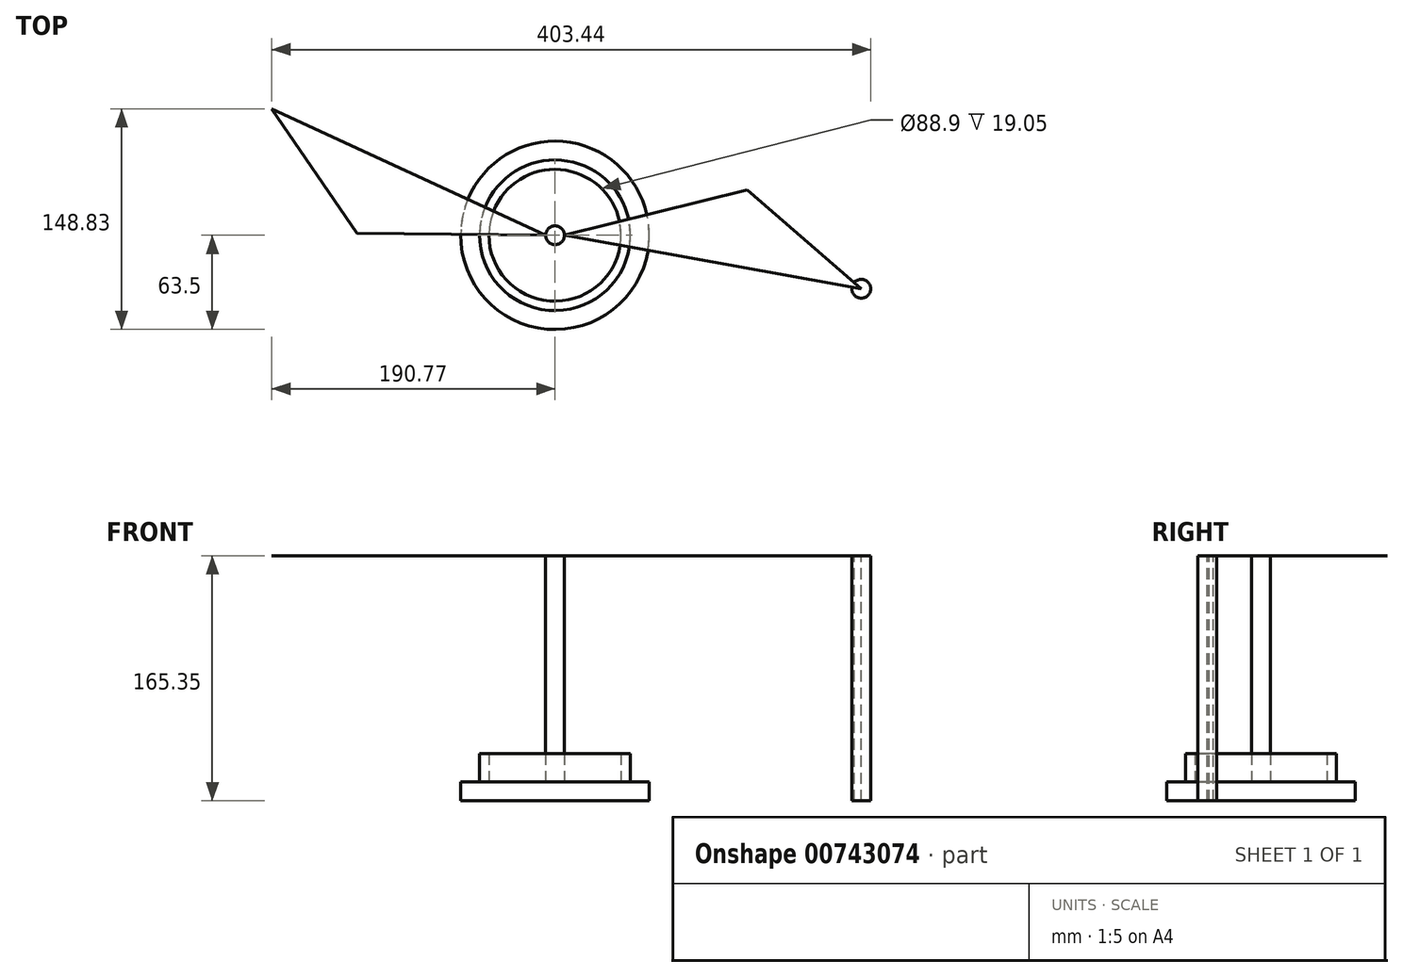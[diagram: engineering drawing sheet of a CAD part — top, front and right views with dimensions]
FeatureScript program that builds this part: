
annotation { "Feature Type Name" : "Feature", "Feature Type Description" : "" }
export const myFeature = defineFeature(function(context is Context, id is Id, definition is map)
    precondition{}
    {
        {
            var Q0;
            Q0=qCreatedBy(makeId("Top.planeOp"),FACE);
            var sketch = newSketch(context, id + "F0", { "sketchPlane" : qUnion([Q0])});
            skCircle(sketch, "E0", {"center": v(0, 0) * mm, "radius": 63.5 * mm});
            skSolve(sketch);
        }
        {
            var Q0;
            Q0 = qSketchRegion(id + "F0", true);
            extrude(context, id + "F1", {"entities" : qUnion([Q0]), "depth" : 12.7 * mm, "offsetDistance" : 25.4 * mm});
        }
        {
            var Q0;
            Q0=qCreatedBy(makeId("Top.planeOp"),FACE);
            var sketch = newSketch(context, id + "F2", { "sketchPlane" : qUnion([Q0])});
            skCircle(sketch, "E1", {"center": v(0, 0) * mm, "radius": 50.8 * mm});
            skCircle(sketch, "E2", {"center": v(0, 0) * mm, "radius": 44.45 * mm});
            skSolve(sketch);
        }
        {
            var Q0;
            Q0 = qSketchRegion(id + "F2", true);
            extrude(context, id + "F3", {"entities" : qUnion([Q0]), "operationType" : NewBodyOperationType.ADD, "depth" : 31.75 * mm, "offsetDistance" : 25.4 * mm});
        }
        {
            var Q0;
            Q0=makeQuery(id+"F3.boolean.opBoolean","SPLIT",FACE,{"disambiguationData":[TD([makeQuery(id+"F3.opExtrude","SWEPT_FACE",FACE,{"disambiguationData":[OSD([sQuery(id+"F2.wireOp",EDGE,"E2")])]})])],"derivedFrom":makeQuery(id+"F1.opExtrude","CAP_FACE",FACE,{"disambiguationData":[OSD([sQuery(id+"F0.wireOp",EDGE,"E0")])],"isStart":false})});
            var sketch = newSketch(context, id + "F4", { "sketchPlane" : qUnion([Q0])});
            skCircle(sketch, "E3", {"center": v(0, 0) * mm, "radius": 6.35 * mm});
            skSolve(sketch);
        }
        {
            var Q0;
            Q0=makeQuery(id+"F4.imprint","IMPRINT",FACE,{"disambiguationData":[TD([[makeQuery(id+"F4.imprint","IMPRINT",EDGE,{"derivedFrom":sQuery(id+"F4.wireOp",EDGE,"E3")}),1.0]])]});
            extrude(context, id + "F5", {"entities" : qUnion([Q0]), "operationType" : NewBodyOperationType.ADD, "depth" : 152.4 * mm, "offsetDistance" : 25.4 * mm});
        }
        {
            var Q0;
            Q0=makeQuery(id+"F5.opExtrude","CAP_FACE",FACE,{"disambiguationData":[OSD([sQuery(id+"F4.wireOp",EDGE,"E3")])],"isStart":false});
            var sketch = newSketch(context, id + "F6", { "sketchPlane" : qUnion([Q0])});
            skLineSegment(sketch, "E4", {"start": v(6.35, 0) * mm, "end": v(129.62, 30.55) * mm});
            skLineSegment(sketch, "E5", {"start": v(6.35, 0) * mm, "end": v(206.32, -36.07) * mm});
            skLineSegment(sketch, "E6", {"start": v(129.62, 30.55) * mm, "end": v(206.32, -36.07) * mm});
            skSolve(sketch);
        }
        {
            var Q0;
            Q0 = qSketchRegion(id + "F6", true);
            extrude(context, id + "F7", {"entities" : qUnion([Q0]), "depth" : 0.25 * mm, "offsetDistance" : 25.4 * mm});
        }
        {
            var Q0;
            Q0=makeQuery(id+"F5.opExtrude","CAP_FACE",FACE,{"disambiguationData":[OSD([sQuery(id+"F4.wireOp",EDGE,"E3")])],"isStart":false});
            var sketch = newSketch(context, id + "F8", { "sketchPlane" : qUnion([Q0])});
            skLineSegment(sketch, "E7", {"start": v(-6.35, 0) * mm, "end": v(-190.77, 85.33) * mm});
            skLineSegment(sketch, "E8", {"start": v(-190.77, 85.33) * mm, "end": v(-133.34, 1.51) * mm});
            skLineSegment(sketch, "E9", {"start": v(-133.34, 1.51) * mm, "end": v(-6.35, 0) * mm});
            skSolve(sketch);
        }
        {
            var Q0;
            Q0=makeQuery(id+"F8.imprint","IMPRINT",FACE,{"disambiguationData":[TD([[makeQuery(id+"F8.imprint","IMPRINT",EDGE,{"derivedFrom":sQuery(id+"F8.wireOp",EDGE,"E7")}),1.0]])]});
            extrude(context, id + "F9", {"entities" : qUnion([Q0]), "depth" : 0.25 * mm, "offsetDistance" : 25.4 * mm});
        }
        {
            var Q0;
            Q0=makeQuery(id+"F9.opExtrude","CAP_FACE",FACE,{"disambiguationData":[OSD([sQuery(id+"F8.wireOp",EDGE,"E7"),sQuery(id+"F8.wireOp",EDGE,"E8"),sQuery(id+"F8.wireOp",EDGE,"E9")])],"isStart":true});
            var sketch = newSketch(context, id + "F10", { "sketchPlane" : qUnion([Q0])});
            skCircle(sketch, "E10", {"center": v(-190.77, -85.33) * mm, "radius": 6.35 * mm});
            skSolve(sketch);
        }
        {
            var Q0;
            Q0=sQuery(id+"F10.wireOp",EDGE,"E10");
            extrude(context, id + "F11", {"bodyType" : ToolBodyType.SURFACE, "surfaceEntities" : qUnion([Q0]), "depth" : 165.1 * mm, "offsetDistance" : 25.4 * mm});
        }
        {
            var Q0;
            Q0=makeQuery(id+"F7.opExtrude","CAP_FACE",FACE,{"disambiguationData":[OSD([sQuery(id+"F6.wireOp",EDGE,"E4"),sQuery(id+"F6.wireOp",EDGE,"E5"),sQuery(id+"F6.wireOp",EDGE,"E6")])],"isStart":true});
            var sketch = newSketch(context, id + "F12", { "sketchPlane" : qUnion([Q0])});
            skCircle(sketch, "E11", {"center": v(206.32, 36.07) * mm, "radius": 6.35 * mm});
            skSolve(sketch);
        }
        {
            var Q0;
            {var subQ0=sQuery(id+"F12.wireOp",EDGE,"E11");var subQ1=makeQuery(id+"F7.opExtrude","CAP_EDGE",EDGE,{"disambiguationData":[OSD([sQuery(id+"F6.wireOp",EDGE,"E5")])],"isStart":true});var subQ2=makeQuery(id+"F12.imprint","INTERSECT",VERTEX,{"derivedFrom":[subQ1,subQ0]});Q0=makeQuery(id+"F12.imprint","IMPRINT",FACE,{"disambiguationData":[TD([[makeQuery(id+"F12.imprint","IMPRINT",EDGE,{"disambiguationData":[TD([[subQ2,1.0]])],"derivedFrom":subQ0}),1.0]])]});}
            extrude(context, id + "F13", {"entities" : qUnion([Q0]), "depth" : 165.1 * mm, "offsetDistance" : 25.4 * mm});
        }
    });
